# Revit family: HSHD-3600D
name_source: partatom
category: Generic Models
units: mm (PartAtom-declared; Revit-internal decimal feet)

## family parameters
Always vertical = Yes
Can host rebar = No
Cut with Voids When Loaded = No
Part Type = Normal
Room Calculation Point = No
Round Connector Dimension = Use Diameter
Shared = No
Work Plane-Based = No

## types (1)
- Standard
    Default Elevation = 0 mm  [stored 0 ft]
    Manufacturer = 三進金属工業株式会社
    URL = https://www.sanshinkinzoku.co.jp
    タイプ = 中央実験台用
    品名 = スチールベンチフード
    品番 = HSHD-3600D
    外寸法　奥行-D = 1480 mm  [stored 4.85564 ft]
    外寸法　間口-W = 3580 mm  [stored 11.7454 ft]
    外寸法　高さ-H = 1600 mm  [stored 5.24934 ft]
    所用ダクト径（φ） = 250mm x 2
    有効内寸法　奥行-D = 1255 mm  [stored 4.11745 ft]
    有効内寸法　間口-W = 3350 mm  [stored 10.9908 ft]
    有効内寸法　高さ-H = 1300 mm  [stored 4.26509 ft]
    本体材質 = スチール（粉体塗装仕上げ）
    本体標準色 = マイルドホワイト
    片面サッシ開口高さ400mm制御風速 = 0.5m/s
    質量 = 741kg
    風量 = 45m3/min

note: [stored X ft] marks values corroborated as IEEE doubles in the binary element streams (Revit-internal decimal feet)

## geometry (parser evidence)
native form markers: Sweep x3
no freeform markers — native parametric forms only
